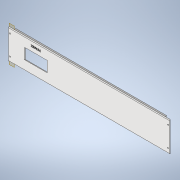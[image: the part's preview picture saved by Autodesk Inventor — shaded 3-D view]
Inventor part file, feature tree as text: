
AUTODESK INVENTOR PART (.ipt)
format: ipt  version: 2022.2 (Build 262287010, 287A)  size: 308,736 bytes
history: native  units: mm
features: reference x13, extrude x4, sketch x4, other x3, plane x1, fillet x1
ambient origin geometry x8: Origin, YZ Plane, XZ Plane, XY Plane, X Axis, Y Axis, Z Axis, Center Point
bodies: Volumenkörper1 (feature_tree)
feature tree (26):
  plane  "Arbeitsebene1"
  extrude  "Extrusion1"  Depth=28.5mm
  extrude  "Extrusion2"  Depth=59.5mm
  extrude  "Extrusion3"  Depth=10.0mm
  extrude  "Extrusion4"  Depth=2.0mm
  fillet  "Rundung1"  Radius=1.0mm
  sketch  "Skizze1"  dims[d0=2.0mm d1=0.0mm d2=28.5mm]
  reference  "Referenz1"
  reference  "Referenz2"
  reference  "Referenz3"
  reference  "Referenz4"
  reference  "Referenz5"
  reference  "Referenz6"
  reference  "Referenz7"
  reference  "Referenz8"
  reference  "Referenz9"
  reference  "Referenz10"
  sketch  "Skizze2"  dims[d3=59.5mm d4=30.0mm]
  reference  "Referenz11"
  sketch  "Skizze3"  dims[d5=2.0mm d6=0.0mm d8=10.0mm]
  sketch  "Skizze4"  dims[d9=0.5mm d10=0.0mm d11=2.0mm d12=1.0mm d13=1.0mm d14=2.0mm d15=1.0mm d16=1.0mm d17=4.0mm d18=0.0mm d19=2.0mm]
  reference  "Referenz12"
  reference  "Referenz13"
  other  "Case_Assembly.iam"
  other  "Case_Side:2"
  other  "Case_Side:1"
